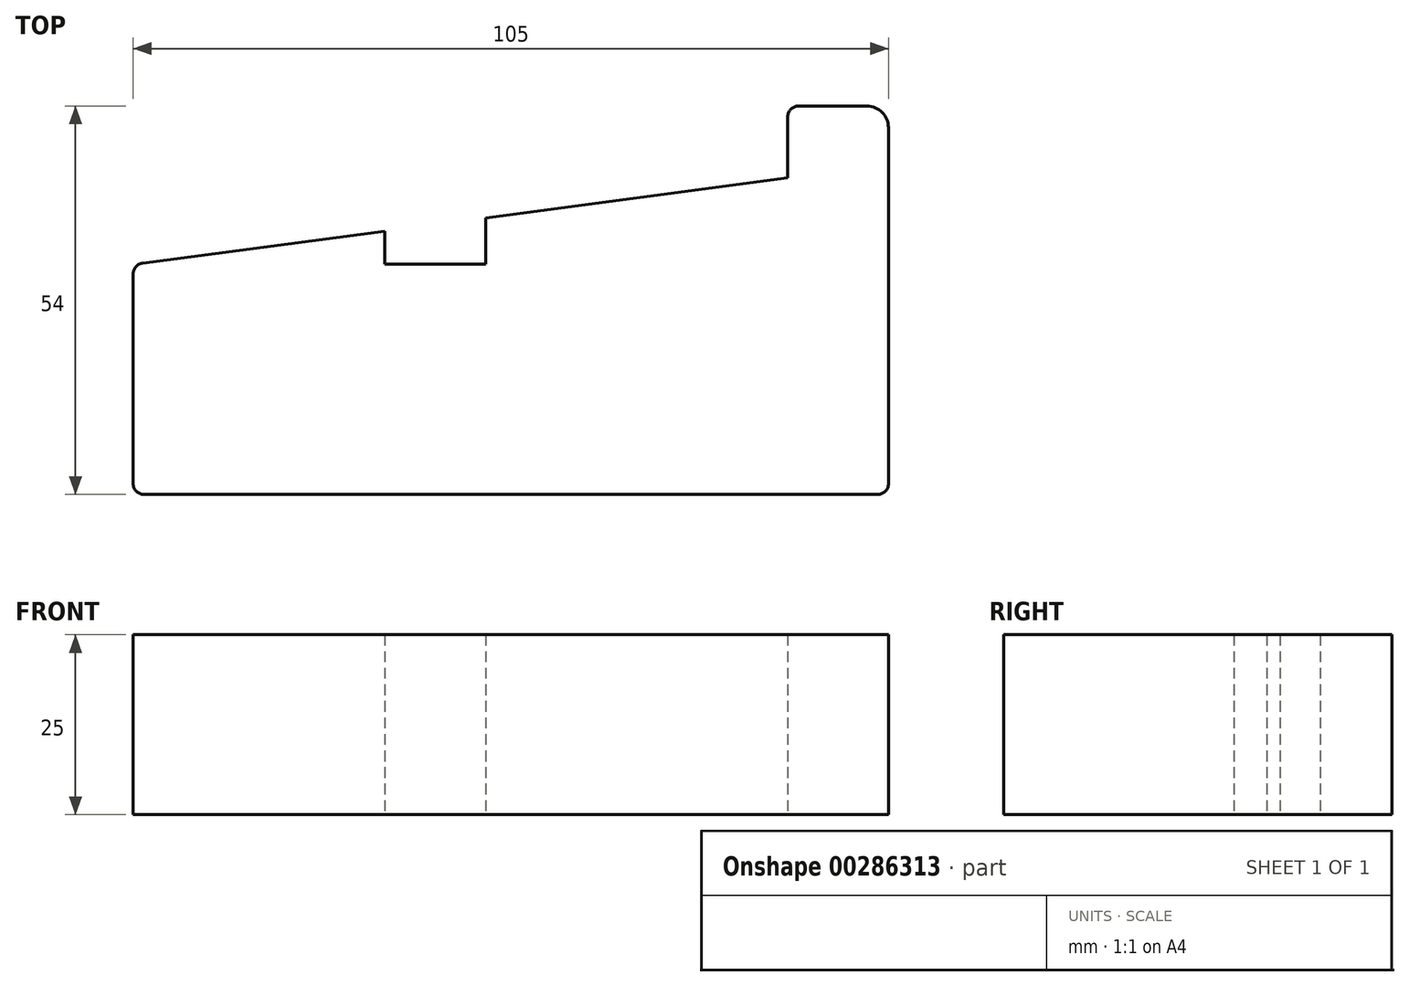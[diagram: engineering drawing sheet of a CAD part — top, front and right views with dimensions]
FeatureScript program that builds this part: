
annotation { "Feature Type Name" : "Feature", "Feature Type Description" : "" }
export const myFeature = defineFeature(function(context is Context, id is Id, definition is map)
    precondition{}
    {
        {
            var Q0;
            Q0=qCreatedBy(makeId("Top.planeOp"),FACE);
            var sketch = newSketch(context, id + "F0", { "sketchPlane" : qUnion([Q0])});
            skLineSegment(sketch, "E0", {"start": v(1.5, 0) * mm, "end": v(103.5, 0) * mm});
            skLineSegment(sketch, "E1", {"start": v(105, 1.5) * mm, "end": v(105, 51) * mm});
            skLineSegment(sketch, "E2", {"start": v(102, 54) * mm, "end": v(92.5, 54) * mm});
            skLineSegment(sketch, "E3", {"start": v(91, 52.5) * mm, "end": v(91, 44) * mm});
            skLineSegment(sketch, "E4", {"start": v(0, 1.5) * mm, "end": v(0, 30.68) * mm});
            skLineSegment(sketch, "E5", {"start": v(35, 32) * mm, "end": v(49, 32) * mm});
            skLineSegment(sketch, "E6", {"start": v(91, 44) * mm, "end": v(49, 38.46) * mm});
            skLineSegment(sketch, "E7", {"start": v(35, 32) * mm, "end": v(35, 36.62) * mm});
            skLineSegment(sketch, "E8", {"start": v(49, 32) * mm, "end": v(49, 38.46) * mm});
            skLineSegment(sketch, "E9.trimOffspring", {"start": v(35, 36.62) * mm, "end": v(1.3, 32.17) * mm});
            skPoint(sketch, "E10.visualSharp", {"position": v(0, 32) * mm});
            skArc(sketch, "E10.filletArc", {"start": v(1.3, 32.17) * mm, "mid": v(0.37, 31.67) * mm, "end": v(0, 30.68) * mm});
            skPoint(sketch, "E11.visualSharp", {"position": v(0, 0) * mm});
            skArc(sketch, "E11.filletArc", {"start": v(0, 1.5) * mm, "mid": v(0.44, 0.44) * mm, "end": v(1.5, 0) * mm});
            skPoint(sketch, "E12.visualSharp", {"position": v(105, 0) * mm});
            skArc(sketch, "E12.filletArc", {"start": v(103.5, 0) * mm, "mid": v(104.56, 0.44) * mm, "end": v(105, 1.5) * mm});
            skPoint(sketch, "E13.visualSharp", {"position": v(91, 54) * mm});
            skArc(sketch, "E13.filletArc", {"start": v(92.5, 54) * mm, "mid": v(91.44, 53.56) * mm, "end": v(91, 52.5) * mm});
            skPoint(sketch, "E14.visualSharp", {"position": v(105, 54) * mm});
            skArc(sketch, "E14.filletArc", {"start": v(105, 51) * mm, "mid": v(104.12, 53.12) * mm, "end": v(102, 54) * mm});
            skSolve(sketch);
        }
        {
            var Q0;
            Q0 = qSketchRegion(id + "F0", true);
            extrude(context, id + "F1", {"entities" : qUnion([Q0]), "depth" : 25 * mm});
        }
    });
